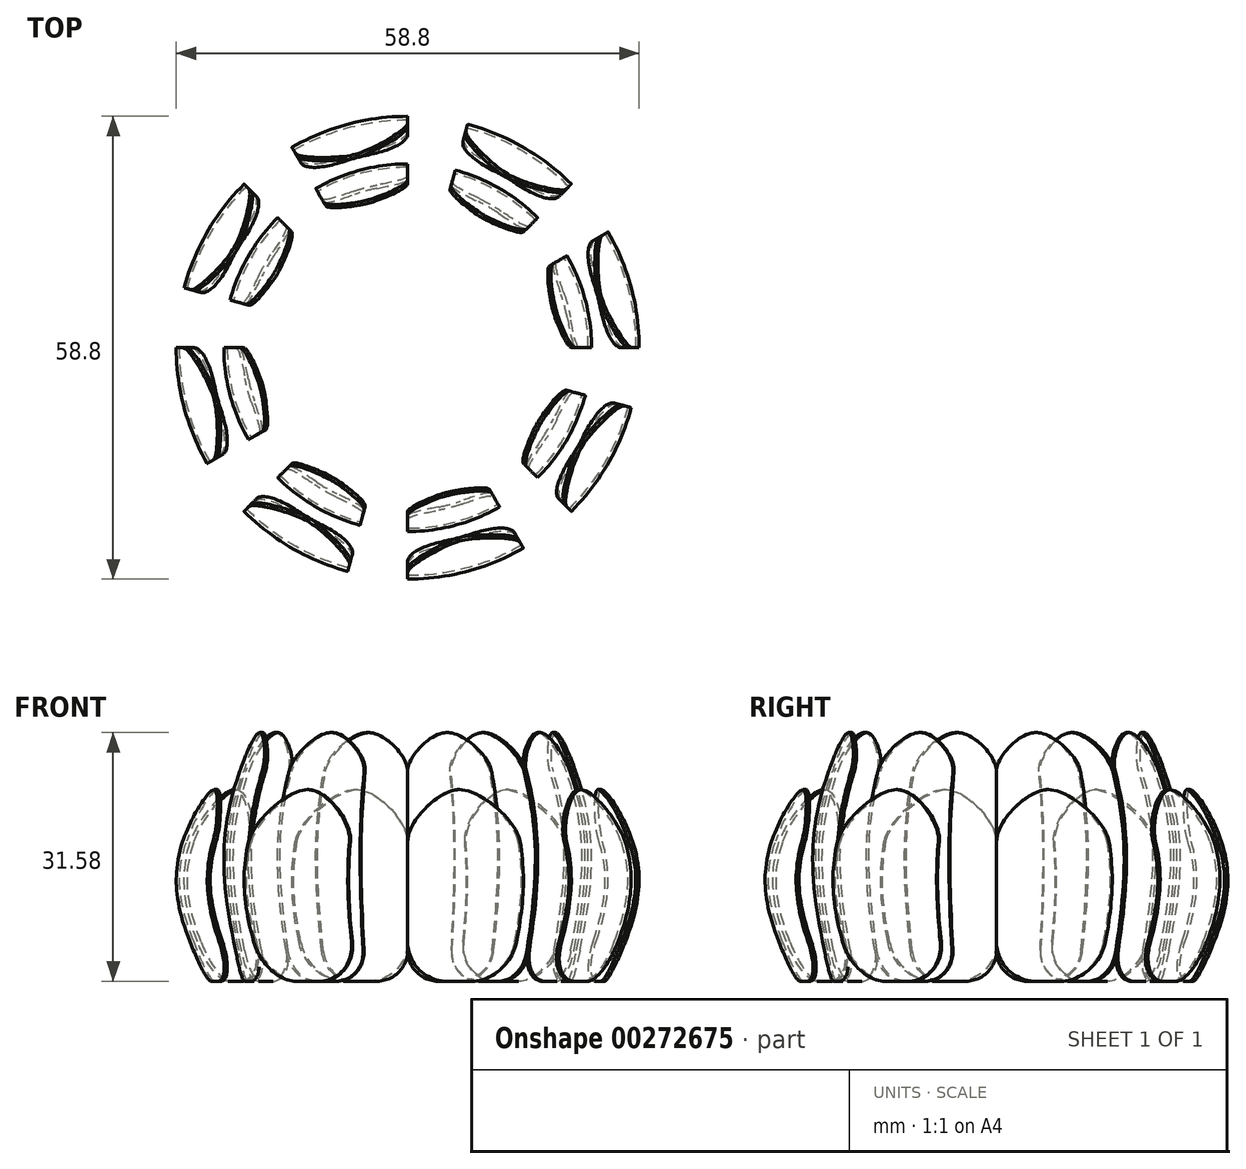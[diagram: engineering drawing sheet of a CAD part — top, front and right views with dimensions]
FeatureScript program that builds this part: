
annotation { "Feature Type Name" : "Feature", "Feature Type Description" : "" }
export const myFeature = defineFeature(function(context is Context, id is Id, definition is map)
    precondition{}
    {
        {
            var Q0;
            Q0=qCreatedBy(makeId("Right.planeOp"),FACE);
            var sketch = newSketch(context, id + "F0", { "sketchPlane" : qUnion([Q0])});
            skLineSegment(sketch, "E0", {"start": v(0, 0) * mm, "end": v(-25, 0) * mm, "construction": true});
            skFitSpline(sketch, "E1", {"points": [v(-25, 0) * mm, v(-28.96, 13.15) * mm, v(-25, 24.35) * mm], "startDerivative": vector(-11.76, 25.94) * mm, "endDerivative": vector(12.05, 22.72) * mm});
            skLineSegment(sketch, "E2", {"start": v(0, 0) * mm, "end": v(0, 14.52) * mm, "construction": true});
            skFitSpline(sketch, "E3.0", {"points": [v(-25.36, -0.17) * mm, v(-25.85, 0.92) * mm, v(-26.84, 3.08) * mm, v(-28.14, 6.33) * mm, v(-28.93, 9) * mm, v(-29.29, 11.13) * mm, v(-29.4, 12.71) * mm, v(-29.32, 14.27) * mm, v(-28.98, 16.31) * mm, v(-28.2, 18.8) * mm, v(-26.86, 21.7) * mm, v(-25.86, 23.6) * mm, v(-25.35, 24.54) * mm]});
            skLineSegment(sketch, "E4", {"start": v(-25, 0) * mm, "end": v(-25.44, 0) * mm});
            skLineSegment(sketch, "E5", {"start": v(-25, 24.35) * mm, "end": v(-25.45, 24.35) * mm});
            skFitSpline(sketch, "E6", {"points": [v(-20.62, 0) * mm, v(-22.86, 17.77) * mm, v(-19.02, 31.58) * mm], "startDerivative": vector(-7.51, 34.83) * mm, "endDerivative": vector(11.06, 28.2) * mm});
            skFitSpline(sketch, "E7.0", {"points": [v(-21, -0.08) * mm, v(-21.32, 1.37) * mm, v(-21.95, 4.27) * mm, v(-22.75, 8.6) * mm, v(-23.2, 12.13) * mm, v(-23.34, 14.89) * mm, v(-23.33, 16.92) * mm, v(-23.18, 18.9) * mm, v(-22.79, 21.48) * mm, v(-22.01, 24.59) * mm, v(-20.77, 28.2) * mm, v(-19.85, 30.55) * mm, v(-19.39, 31.72) * mm]});
            skLineSegment(sketch, "E8", {"start": v(-19.02, 31.58) * mm, "end": v(-19.45, 31.58) * mm});
            skLineSegment(sketch, "E9", {"start": v(-20.62, 0) * mm, "end": v(-21.03, 0) * mm});
            skSolve(sketch);
        }
        {
            var Q0;
            Q0=makeQuery(id+"F0.imprint","IMPRINT",FACE,{"disambiguationData":[TD([[makeQuery(id+"F0.imprint","IMPRINT",EDGE,{"derivedFrom":sQuery(id+"F0.wireOp",EDGE,"E1")}),1.0]])]});
            var Q1;
            Q1=makeQuery(id+"F0.imprint","IMPRINT",FACE,{"disambiguationData":[TD([[makeQuery(id+"F0.imprint","IMPRINT",EDGE,{"derivedFrom":sQuery(id+"F0.wireOp",EDGE,"E6")}),1.0]])]});
            var Q2;
            Q2=sQuery(id+"F0.wireOp",EDGE,"E1");
            var Q3;
            Q3=sQuery(id+"F0.wireOp",EDGE,"E2");
            revolve(context, id + "F1", {"entities" : qUnion([Q0, Q1]), "surfaceEntities" : qUnion([Q2]), "axis" : qUnion([Q3]), "revolveType" : RevolveType.ONE_DIRECTION, "angle" : 30 * degree});
        }
        {
            var Q0;
            Q0=makeQuery(id+"F1.opRevolve","CAP_EDGE",EDGE,{"disambiguationData":[OSD([sQuery(id+"F0.wireOp",EDGE,"E5")])],"isStart":false});
            var Q1;
            Q1=makeQuery(id+"F1.opRevolve","CAP_EDGE",EDGE,{"disambiguationData":[OSD([sQuery(id+"F0.wireOp",EDGE,"E5")])],"isStart":true});
            fillet(context, id + "F2", {"entities" : qUnion([Q0, Q1]), "radius" : 6.6 * mm, "tangentPropagation" : true, "rho" : 0.3, "crossSection" : FilletCrossSection.CONIC, "allowEdgeOverflow" : false});
        }
        {
            var Q0;
            Q0=makeQuery(id+"F1.opRevolve","CAP_EDGE",EDGE,{"disambiguationData":[OSD([sQuery(id+"F0.wireOp",EDGE,"E4")])],"isStart":false});
            var Q1;
            Q1=makeQuery(id+"F1.opRevolve","CAP_EDGE",EDGE,{"disambiguationData":[OSD([sQuery(id+"F0.wireOp",EDGE,"E4")])],"isStart":true});
            fillet(context, id + "F3", {"entities" : qUnion([Q0, Q1]), "radius" : 5 * mm, "tangentPropagation" : true, "allowEdgeOverflow" : false});
        }
        {
            var Q0;
            Q0=makeQuery(id+"F1.opRevolve","CAP_EDGE",EDGE,{"disambiguationData":[OSD([sQuery(id+"F0.wireOp",EDGE,"E8")])],"isStart":true});
            var Q1;
            Q1=makeQuery(id+"F1.opRevolve","CAP_EDGE",EDGE,{"disambiguationData":[OSD([sQuery(id+"F0.wireOp",EDGE,"E8")])],"isStart":false});
            fillet(context, id + "F4", {"entities" : qUnion([Q0, Q1]), "radius" : 4.9 * mm, "tangentPropagation" : true, "rho" : 0.3, "crossSection" : FilletCrossSection.CONIC, "allowEdgeOverflow" : false});
        }
        {
            var Q0;
            Q0=makeQuery(id+"F1.opRevolve","CAP_EDGE",EDGE,{"disambiguationData":[OSD([sQuery(id+"F0.wireOp",EDGE,"E9")])],"isStart":true});
            var Q1;
            Q1=makeQuery(id+"F1.opRevolve","CAP_EDGE",EDGE,{"disambiguationData":[OSD([sQuery(id+"F0.wireOp",EDGE,"E9")])],"isStart":false});
            fillet(context, id + "F5", {"entities" : qUnion([Q0, Q1]), "radius" : 3.9 * mm, "tangentPropagation" : true, "allowEdgeOverflow" : false});
        }
        {
            var Q0;
            Q0=makeQuery(id+"F1.opRevolve","SWEPT_BODY",BODY,{"disambiguationData":[OSD([sQuery(id+"F0.wireOp",EDGE,"E1"),sQuery(id+"F0.wireOp",EDGE,"E3.0"),sQuery(id+"F0.wireOp",EDGE,"E4"),sQuery(id+"F0.wireOp",EDGE,"E5")])]});
            var Q1;
            Q1=makeQuery(id+"F1.opRevolve","SWEPT_BODY",BODY,{"disambiguationData":[OSD([sQuery(id+"F0.wireOp",EDGE,"E6"),sQuery(id+"F0.wireOp",EDGE,"E7.0"),sQuery(id+"F0.wireOp",EDGE,"E8"),sQuery(id+"F0.wireOp",EDGE,"E9")])]});
            var Q2;
            Q2=sQuery(id+"F0.wireOp",EDGE,"E2");
            circularPattern(context, id + "F6", {"entities" : qUnion([Q0, Q1]), "axis" : qUnion([Q2]), "angle" : 360 * degree, "instanceCount" : 8, "equalSpace" : true});
        }
    });
